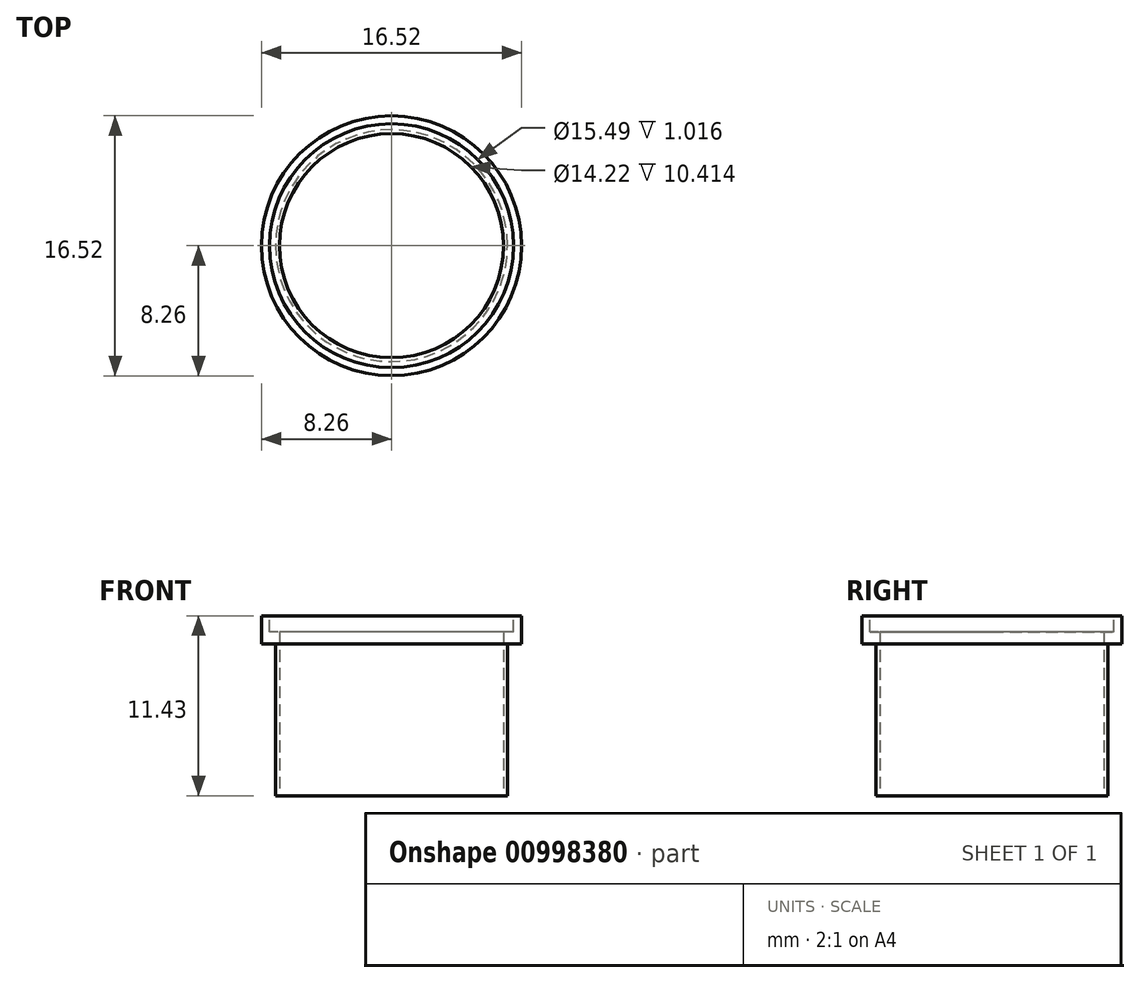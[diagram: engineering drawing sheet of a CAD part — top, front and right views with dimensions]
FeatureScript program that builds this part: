
annotation { "Feature Type Name" : "Feature", "Feature Type Description" : "" }
export const myFeature = defineFeature(function(context is Context, id is Id, definition is map)
    precondition{}
    {
        {
            var Q0;
            Q0=qCreatedBy(makeId("Top.planeOp"),FACE);
            var sketch = newSketch(context, id + "F0", { "sketchPlane" : qUnion([Q0])});
            skCircle(sketch, "E0", {"center": v(0, 0) * mm, "radius": 7.11 * mm});
            skSolve(sketch);
        }
        {
            var Q0;
            Q0=qCreatedBy(makeId("Top.planeOp"),FACE);
            var sketch = newSketch(context, id + "F1", { "sketchPlane" : qUnion([Q0])});
            skCircle(sketch, "E1", {"center": v(0, 0) * mm, "radius": 7.37 * mm});
            skSolve(sketch);
        }
        {
            var Q0;
            Q0 = qSketchRegion(id + "F1", true);
            extrude(context, id + "F2", {"entities" : qUnion([Q0]), "depth" : 9.65 * mm, "offsetDistance" : 25.4 * mm});
        }
        {
            var Q0;
            Q0=makeQuery(id+"F2.opExtrude","CAP_FACE",FACE,{"disambiguationData":[OSD([sQuery(id+"F1.wireOp",EDGE,"E1")])],"isStart":false});
            var sketch = newSketch(context, id + "F3", { "sketchPlane" : qUnion([Q0])});
            skCircle(sketch, "E2", {"center": v(0, 0) * mm, "radius": 8.26 * mm});
            skSolve(sketch);
        }
        {
            var Q0;
            Q0 = qSketchRegion(id + "F3", true);
            extrude(context, id + "F4", {"entities" : qUnion([Q0]), "operationType" : NewBodyOperationType.ADD, "depth" : 1.78 * mm, "offsetDistance" : 25.4 * mm});
        }
        {
            var Q0;
            Q0=makeQuery(id+"F4.opExtrude","CAP_FACE",FACE,{"disambiguationData":[OSD([sQuery(id+"F3.wireOp",EDGE,"E2")])],"isStart":false});
            var sketch = newSketch(context, id + "F5", { "sketchPlane" : qUnion([Q0])});
            skCircle(sketch, "E3", {"center": v(0, 0) * mm, "radius": 7.75 * mm});
            skSolve(sketch);
        }
        {
            var Q0;
            Q0 = qSketchRegion(id + "F5", true);
            extrude(context, id + "F6", {"entities" : qUnion([Q0]), "operationType" : NewBodyOperationType.REMOVE, "oppositeDirection" : true, "depth" : 1.02 * mm, "offsetDistance" : 25.4 * mm});
        }
        {
            var Q0;
            Q0 = qSketchRegion(id + "F0", true);
            extrude(context, id + "F7", {"entities" : qUnion([Q0]), "operationType" : NewBodyOperationType.REMOVE, "depth" : 19.3 * mm, "offsetDistance" : 25.4 * mm});
        }
    });
